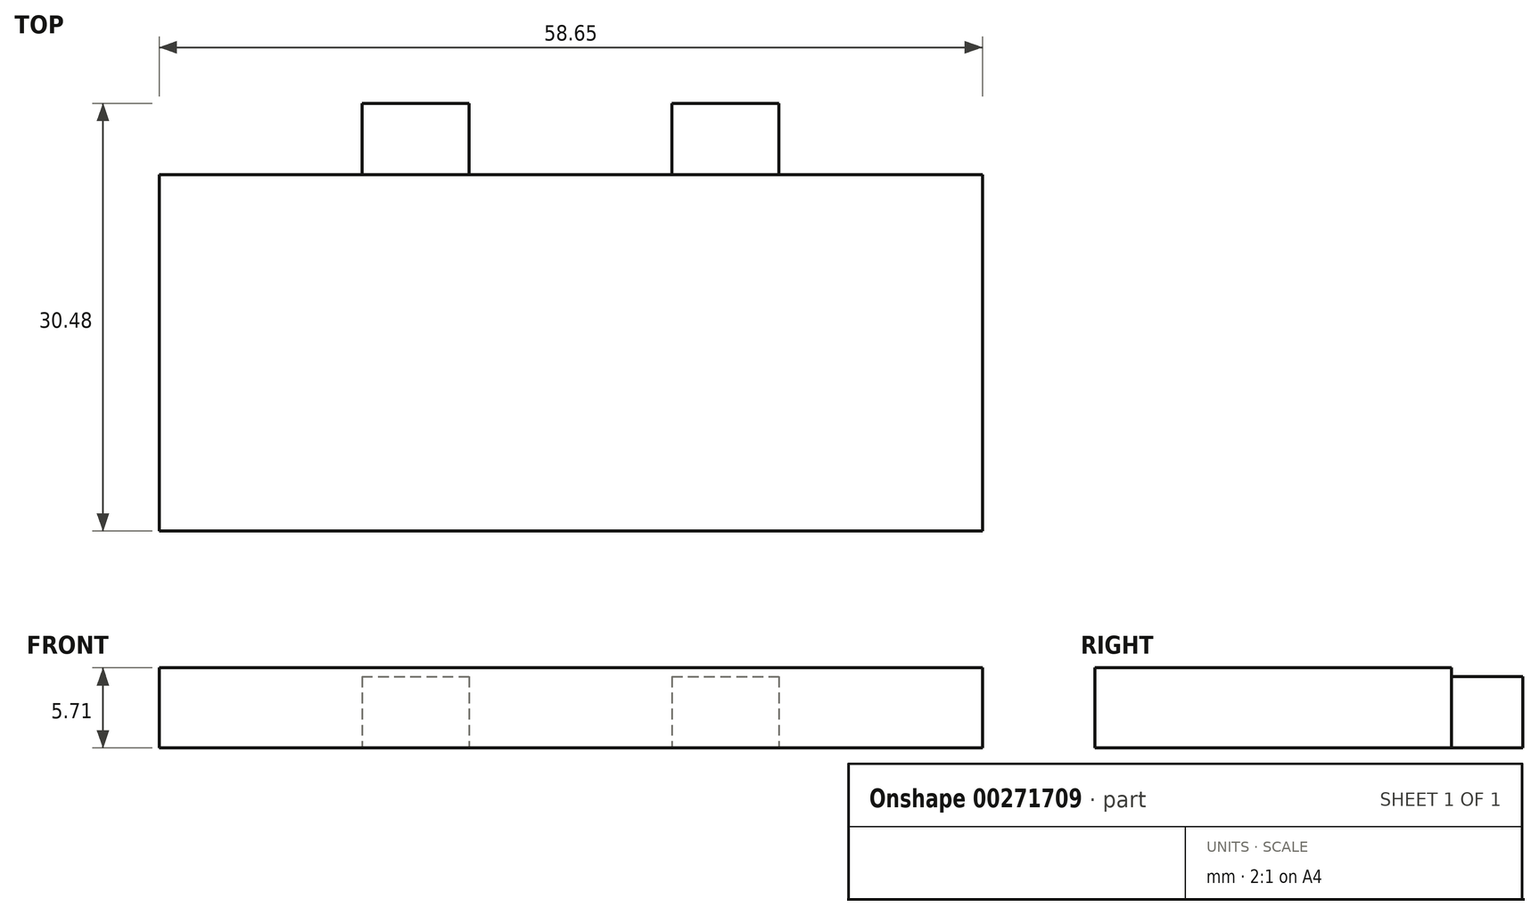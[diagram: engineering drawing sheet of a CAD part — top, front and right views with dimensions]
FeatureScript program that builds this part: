
annotation { "Feature Type Name" : "Feature", "Feature Type Description" : "" }
export const myFeature = defineFeature(function(context is Context, id is Id, definition is map)
    precondition{}
    {
        {
            var Q0;
            Q0=qCreatedBy(makeId("Top.planeOp"),FACE);
            var sketch = newSketch(context, id + "F0", { "sketchPlane" : qUnion([Q0])});
            skLineSegment(sketch, "E0.bottom", {"start": v(-51.46, 21.77) * mm, "end": v(7.19, 21.77) * mm});
            skLineSegment(sketch, "E0.top", {"start": v(-51.46, -3.63) * mm, "end": v(7.19, -3.63) * mm});
            skLineSegment(sketch, "E0.left", {"start": v(-51.46, 21.77) * mm, "end": v(-51.46, -3.63) * mm});
            skLineSegment(sketch, "E0.right", {"start": v(7.19, 21.77) * mm, "end": v(7.19, -3.63) * mm});
            skLineSegment(sketch, "E1", {"start": v(-37, 21.77) * mm, "end": v(-37, 26.85) * mm});
            skLineSegment(sketch, "E2", {"start": v(-37, 26.85) * mm, "end": v(-29.39, 26.85) * mm});
            skLineSegment(sketch, "E3", {"start": v(-29.39, 26.85) * mm, "end": v(-29.39, 21.77) * mm});
            skLineSegment(sketch, "E4", {"start": v(-14.94, 21.77) * mm, "end": v(-14.94, 26.85) * mm});
            skLineSegment(sketch, "E5", {"start": v(-14.94, 26.85) * mm, "end": v(-7.32, 26.85) * mm});
            skLineSegment(sketch, "E6", {"start": v(-7.32, 26.85) * mm, "end": v(-7.32, 21.77) * mm});
            skLineSegment(sketch, "E7", {"start": v(-51.46, 21.77) * mm, "end": v(-51.46, 47.3) * mm, "construction": true});
            skLineSegment(sketch, "E8", {"start": v(7.19, 21.77) * mm, "end": v(7.19, 41.25) * mm, "construction": true});
            skSolve(sketch);
        }
        {
            var Q0;
            Q0=makeQuery(id+"F0.imprint","IMPRINT",FACE,{"disambiguationData":[TD([[makeQuery(id+"F0.imprint","IMPRINT",EDGE,{"derivedFrom":sQuery(id+"F0.wireOp",EDGE,"E0.top")}),1.0]])]});
            extrude(context, id + "F1", {"entities" : qUnion([Q0]), "depth" : 5.7 * mm});
        }
        {
            var Q0;
            {var subQ0=sQuery(id+"F0.wireOp",EDGE,"E1");Q0=makeQuery(id+"F0.imprint","IMPRINT",FACE,{"disambiguationData":[TD([[makeQuery(id+"F0.imprint","IMPRINT",EDGE,{"derivedFrom":subQ0}),-1.0]])]});}
            var Q1;
            {var subQ0=sQuery(id+"F0.wireOp",EDGE,"E4");Q1=makeQuery(id+"F0.imprint","IMPRINT",FACE,{"disambiguationData":[TD([[makeQuery(id+"F0.imprint","IMPRINT",EDGE,{"derivedFrom":subQ0}),-1.0]])]});}
            extrude(context, id + "F2", {"entities" : qUnion([Q0, Q1]), "operationType" : NewBodyOperationType.ADD, "depth" : 5.08 * mm});
        }
    });
